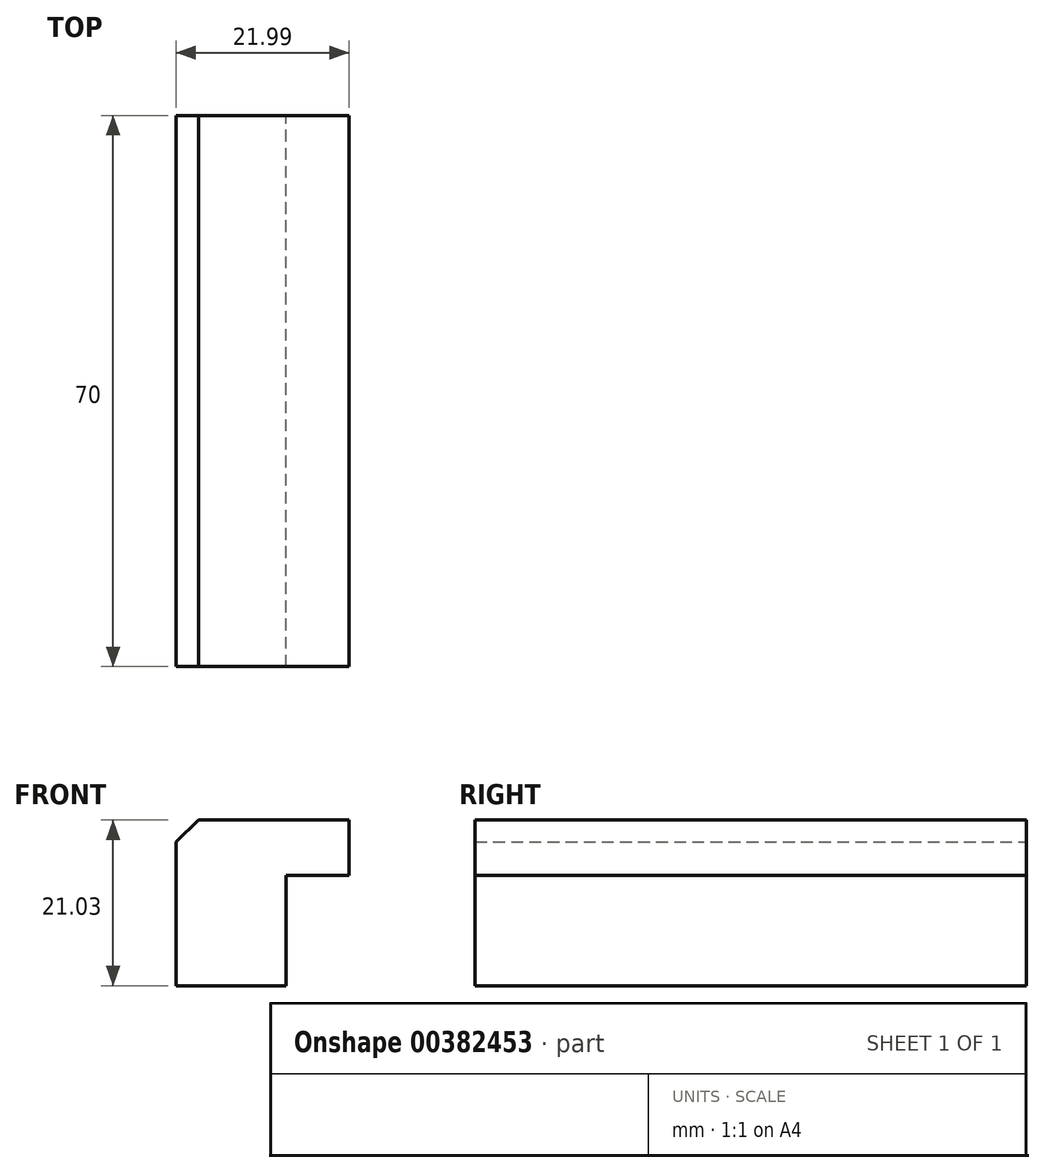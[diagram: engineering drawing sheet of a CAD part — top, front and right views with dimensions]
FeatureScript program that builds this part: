
annotation { "Feature Type Name" : "Feature", "Feature Type Description" : "" }
export const myFeature = defineFeature(function(context is Context, id is Id, definition is map)
    precondition{}
    {
        {
            var Q0;
            Q0=qCreatedBy(makeId("Front.planeOp"),FACE);
            var sketch = newSketch(context, id + "F0", { "sketchPlane" : qUnion([Q0])});
            skLineSegment(sketch, "E0", {"start": v(-38.54, 25.15) * mm, "end": v(-24.55, 25.15) * mm});
            skLineSegment(sketch, "E1", {"start": v(-24.55, 25.15) * mm, "end": v(-24.55, 39.14) * mm});
            skLineSegment(sketch, "E2", {"start": v(-24.55, 39.14) * mm, "end": v(-16.55, 39.14) * mm});
            skLineSegment(sketch, "E3", {"start": v(-16.55, 39.14) * mm, "end": v(-16.55, 46.18) * mm});
            skLineSegment(sketch, "E4", {"start": v(-16.55, 46.18) * mm, "end": v(-35.66, 46.18) * mm});
            skLineSegment(sketch, "E5", {"start": v(-35.66, 46.18) * mm, "end": v(-38.54, 43.43) * mm});
            skPoint(sketch, "E6.end.orphan", {"position": v(-38.54, 39.14) * mm});
            skLineSegment(sketch, "E7", {"start": v(-38.54, 43.43) * mm, "end": v(-38.54, 25.15) * mm});
            skSolve(sketch);
        }
        {
            var Q0;
            Q0 = qSketchRegion(id + "F0", true);
            extrude(context, id + "F1", {"entities" : qUnion([Q0]), "depth" : 70 * mm});
        }
    });
